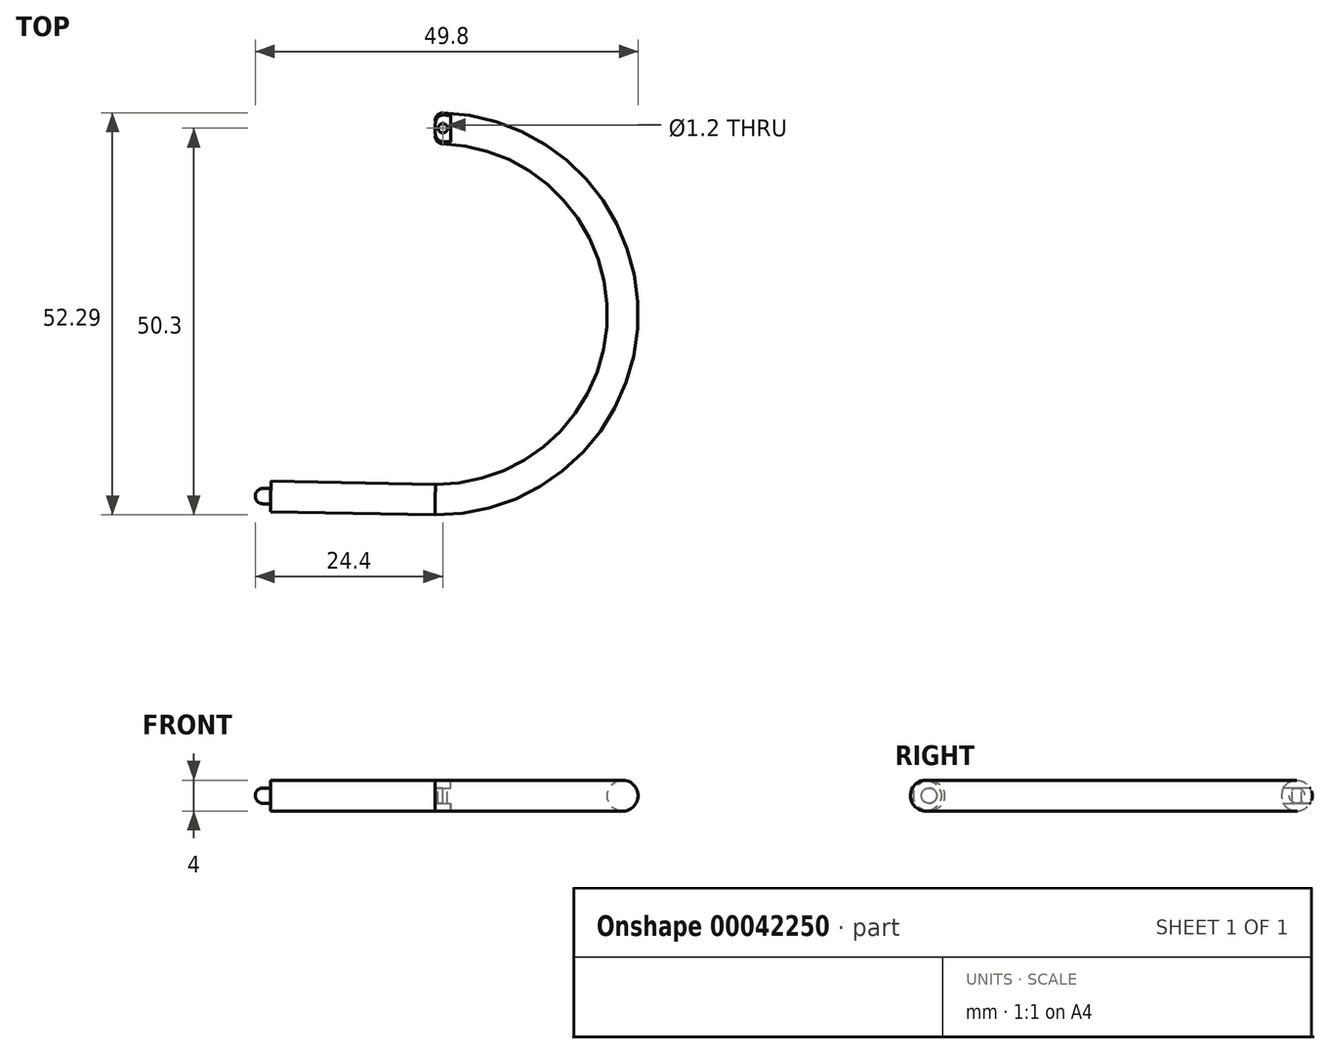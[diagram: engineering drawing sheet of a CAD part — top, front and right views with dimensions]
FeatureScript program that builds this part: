
annotation { "Feature Type Name" : "Feature", "Feature Type Description" : "" }
export const myFeature = defineFeature(function(context is Context, id is Id, definition is map)
    precondition{}
    {
        {
            var Q0;
            Q0=qCreatedBy(makeId("Right.planeOp"),FACE);
            var sketch = newSketch(context, id + "F0", { "sketchPlane" : qUnion([Q0])});
            skCircle(sketch, "E0", {"center": v(0, 0) * mm, "radius": 2 * mm});
            skSolve(sketch);
        }
        {
            var Q0;
            Q0=qCreatedBy(makeId("Top.planeOp"),FACE);
            var sketch = newSketch(context, id + "F1", { "sketchPlane" : qUnion([Q0])});
            skArc(sketch, "E1", {"start": v(0, -48.3) * mm, "mid": v(24.4, -24.15) * mm, "end": v(0, 0) * mm});
            skSolve(sketch);
        }
        {
            var Q0;
            Q0=makeQuery(id+"F0.imprint","IMPRINT",FACE,{"disambiguationData":[TD([[makeQuery(id+"F0.imprint","IMPRINT",EDGE,{"derivedFrom":sQuery(id+"F0.wireOp",EDGE,"E0")}),1.0]])]});
            var Q1;
            Q1=sQuery(id+"F1.wireOp",EDGE,"E1");
            sweep(context, id + "F2", {"profiles" : qUnion([Q0]), "path" : qUnion([Q1])});
        }
        {
            var Q0;
            Q0=makeQuery(id+"F2.opSweep","CAP_FACE",FACE,{"disambiguationData":[OSD([sQuery(id+"F0.wireOp",EDGE,"E0"),sQuery(id+"F1.wireOp",VERTEX,"E1.start")])],"isStart":false});
            var sketch = newSketch(context, id + "F3", { "sketchPlane" : qUnion([Q0])});
            skCircle(sketch, "E2", {"center": v(48.3, 0) * mm, "radius": 2 * mm});
            skSolve(sketch);
        }
        {
            var Q0;
            Q0 = qSketchRegion(id + "F3", true);
            extrude(context, id + "F4", {"entities" : qUnion([Q0]), "operationType" : NewBodyOperationType.ADD, "depth" : 21.4 * mm});
        }
        {
            var Q0;
            Q0=makeQuery(id+"F4.opExtrude","CAP_FACE",FACE,{"disambiguationData":[OSD([sQuery(id+"F3.wireOp",EDGE,"E2")])],"isStart":false});
            var sketch = newSketch(context, id + "F5", { "sketchPlane" : qUnion([Q0])});
            skCircle(sketch, "E3", {"center": v(48.3, 0) * mm, "radius": 1 * mm});
            skSolve(sketch);
        }
        {
            var Q0;
            Q0 = qSketchRegion(id + "F5", true);
            extrude(context, id + "F6", {"entities" : qUnion([Q0]), "operationType" : NewBodyOperationType.ADD, "depth" : 2 * mm});
        }
        {
            var Q0;
            Q0=makeQuery(id+"F6.opExtrude","CAP_EDGE",EDGE,{"disambiguationData":[OSD([sQuery(id+"F5.wireOp",EDGE,"E3")])],"isStart":false});
            fillet(context, id + "F7", {"entities" : qUnion([Q0]), "radius" : 1 * mm, "tangentPropagation" : true, "allowEdgeOverflow" : false});
        }
        {
            var Q0;
            Q0=qCreatedBy(makeId("Top.planeOp"),FACE);
            var sketch = newSketch(context, id + "F8", { "sketchPlane" : qUnion([Q0])});
            skLineSegment(sketch, "E4", {"start": v(0, 0) * mm, "end": v(1, 0) * mm, "construction": true});
            skCircle(sketch, "E5", {"center": v(1, 0) * mm, "radius": 0.6 * mm});
            skSolve(sketch);
        }
        {
            var Q0;
            Q0 = qSketchRegion(id + "F8", true);
            extrude(context, id + "F9", {"entities" : qUnion([Q0]), "operationType" : NewBodyOperationType.REMOVE, "oppositeDirection" : true, "depth" : 25 * mm});
        }
        {
            var Q0;
            Q0=makeQuery(id+"F9.boolean.opBoolean","COPY",FACE,{"derivedFrom":makeQuery(id+"F9.opExtrude","CAP_FACE",FACE,{"disambiguationData":[OSD([sQuery(id+"F8.wireOp",EDGE,"E5")])],"isStart":true})});
            var sketch = newSketch(context, id + "F10", { "sketchPlane" : qUnion([Q0])});
            skCircle(sketch, "E6", {"center": v(1, 0) * mm, "radius": 0.6 * mm});
            skSolve(sketch);
        }
        {
            var Q0;
            Q0 = qSketchRegion(id + "F10", true);
            extrude(context, id + "F11", {"entities" : qUnion([Q0]), "operationType" : NewBodyOperationType.REMOVE, "oppositeDirection" : true, "depth" : 9.02 * mm});
        }
        {
            var Q0;
            Q0=qCreatedBy(makeId("Front.planeOp"),FACE);
            var sketch = newSketch(context, id + "F12", { "sketchPlane" : qUnion([Q0])});
            skLineSegment(sketch, "E7", {"start": v(0, 0) * mm, "end": v(0, 1) * mm});
            skLineSegment(sketch, "E8", {"start": v(0, 1) * mm, "end": v(2, 1) * mm});
            skLineSegment(sketch, "E9", {"start": v(2, 1) * mm, "end": v(2, 2.17) * mm});
            skLineSegment(sketch, "E10", {"start": v(2, 2.17) * mm, "end": v(0, 2.17) * mm});
            skLineSegment(sketch, "E11", {"start": v(0, 2.17) * mm, "end": v(0, 1) * mm});
            skLineSegment(sketch, "E12", {"start": v(0, 0) * mm, "end": v(0, -1) * mm});
            skLineSegment(sketch, "E13", {"start": v(0, -1) * mm, "end": v(2, -1) * mm});
            skLineSegment(sketch, "E14", {"start": v(2, -1) * mm, "end": v(2, -2.25) * mm});
            skLineSegment(sketch, "E15", {"start": v(2, -2.25) * mm, "end": v(0, -2.25) * mm});
            skLineSegment(sketch, "E16", {"start": v(0, -2.25) * mm, "end": v(0, -1) * mm});
            skSolve(sketch);
        }
        {
            var Q0;
            Q0 = qSketchRegion(id + "F12", true);
            extrude(context, id + "F13", {"entities" : qUnion([Q0]), "operationType" : NewBodyOperationType.REMOVE, "oppositeDirection" : true, "depth" : 25 * mm});
        }
        {
            var Q0;
            {var subQ0=sQuery(id+"F12.wireOp",EDGE,"E8");var subQ1=sQuery(id+"F12.wireOp",EDGE,"E9");Q0=makeQuery(id+"F13.boolean.opBoolean","COPY",FACE,{"disambiguationData":[TD([makeQuery(id+"F13.opExtrude","SWEPT_FACE",FACE,{"disambiguationData":[OSD([subQ1])]})])],"derivedFrom":makeQuery(id+"F13.opExtrude","CAP_FACE",FACE,{"disambiguationData":[OSD([subQ0,subQ1,sQuery(id+"F12.wireOp",EDGE,"E10"),sQuery(id+"F12.wireOp",EDGE,"E11")])],"isStart":true})});}
            var sketch = newSketch(context, id + "F14", { "sketchPlane" : qUnion([Q0])});
            skLineSegment(sketch, "E17.bottom", {"start": v(-2, 1) * mm, "end": v(0, 1) * mm});
            skLineSegment(sketch, "E17.top", {"start": v(-2, 3.09) * mm, "end": v(0, 3.09) * mm});
            skLineSegment(sketch, "E17.left", {"start": v(-2, 1) * mm, "end": v(-2, 3.09) * mm});
            skLineSegment(sketch, "E17.right", {"start": v(0, 1) * mm, "end": v(0, 3.09) * mm});
            skSolve(sketch);
        }
        {
            var Q0;
            Q0 = qSketchRegion(id + "F14", true);
            extrude(context, id + "F15", {"entities" : qUnion([Q0]), "operationType" : NewBodyOperationType.REMOVE, "oppositeDirection" : true, "depth" : 25 * mm});
        }
        {
            var Q0;
            {var subQ0=sQuery(id+"F0.wireOp",EDGE,"E0");var subQ1=sQuery(id+"F12.wireOp",EDGE,"E13");Q0=makeQuery(id+"F13.boolean.opBoolean","COPY",FACE,{"disambiguationData":[TD([makeQuery(id+"F2.opSweep","CAP_FACE",FACE,{"disambiguationData":[OSD([subQ0,sQuery(id+"F1.wireOp",VERTEX,"E1.end")])],"isStart":true})])],"derivedFrom":makeQuery(id+"F13.opExtrude","CAP_FACE",FACE,{"disambiguationData":[OSD([subQ1,sQuery(id+"F12.wireOp",EDGE,"E14"),sQuery(id+"F12.wireOp",EDGE,"E15"),sQuery(id+"F12.wireOp",EDGE,"E16")])],"isStart":true})});}
            var sketch = newSketch(context, id + "F16", { "sketchPlane" : qUnion([Q0])});
            skLineSegment(sketch, "E18.bottom", {"start": v(0, -2) * mm, "end": v(-2, -2) * mm});
            skLineSegment(sketch, "E18.top", {"start": v(0, -1) * mm, "end": v(-2, -1) * mm});
            skLineSegment(sketch, "E18.left", {"start": v(0, -2) * mm, "end": v(0, -1) * mm});
            skLineSegment(sketch, "E18.right", {"start": v(-2, -2) * mm, "end": v(-2, -1) * mm});
            skSolve(sketch);
        }
        {
            var Q0;
            Q0 = qSketchRegion(id + "F16", true);
            extrude(context, id + "F17", {"entities" : qUnion([Q0]), "operationType" : NewBodyOperationType.REMOVE, "oppositeDirection" : true, "depth" : 25 * mm});
        }
        {
            var Q0;
            {var subQ0=sQuery(id+"F1.wireOp",VERTEX,"E1.end");var subQ1=sQuery(id+"F0.wireOp",EDGE,"E0");Q0=makeQuery(id+"F13.boolean.opBoolean","SPLIT",EDGE,{"disambiguationData":[TD([makeQuery(id+"F13.opExtrude","CAP_FACE",FACE,{"disambiguationData":[OSD([sQuery(id+"F12.wireOp",EDGE,"E8"),sQuery(id+"F12.wireOp",EDGE,"E9"),sQuery(id+"F12.wireOp",EDGE,"E10"),sQuery(id+"F12.wireOp",EDGE,"E11")])],"isStart":true})])],"derivedFrom":makeQuery(id+"F2.opSweep","CAP_EDGE",EDGE,{"disambiguationData":[OSD([subQ1,subQ0])],"isStart":true})});}
            var Q1;
            {var subQ0=sQuery(id+"F1.wireOp",VERTEX,"E1.end");var subQ1=sQuery(id+"F0.wireOp",EDGE,"E0");Q1=makeQuery(id+"F13.boolean.opBoolean","SPLIT",EDGE,{"disambiguationData":[TD([makeQuery(id+"F13.opExtrude","SWEPT_FACE",FACE,{"disambiguationData":[OSD([sQuery(id+"F12.wireOp",EDGE,"E8")])]})])],"derivedFrom":makeQuery(id+"F2.opSweep","CAP_EDGE",EDGE,{"disambiguationData":[OSD([subQ1,subQ0])],"isStart":true})});}
            fillet(context, id + "F18", {"entities" : qUnion([Q0, Q1]), "radius" : 1 * mm, "tangentPropagation" : true, "allowEdgeOverflow" : false});
        }
    });
